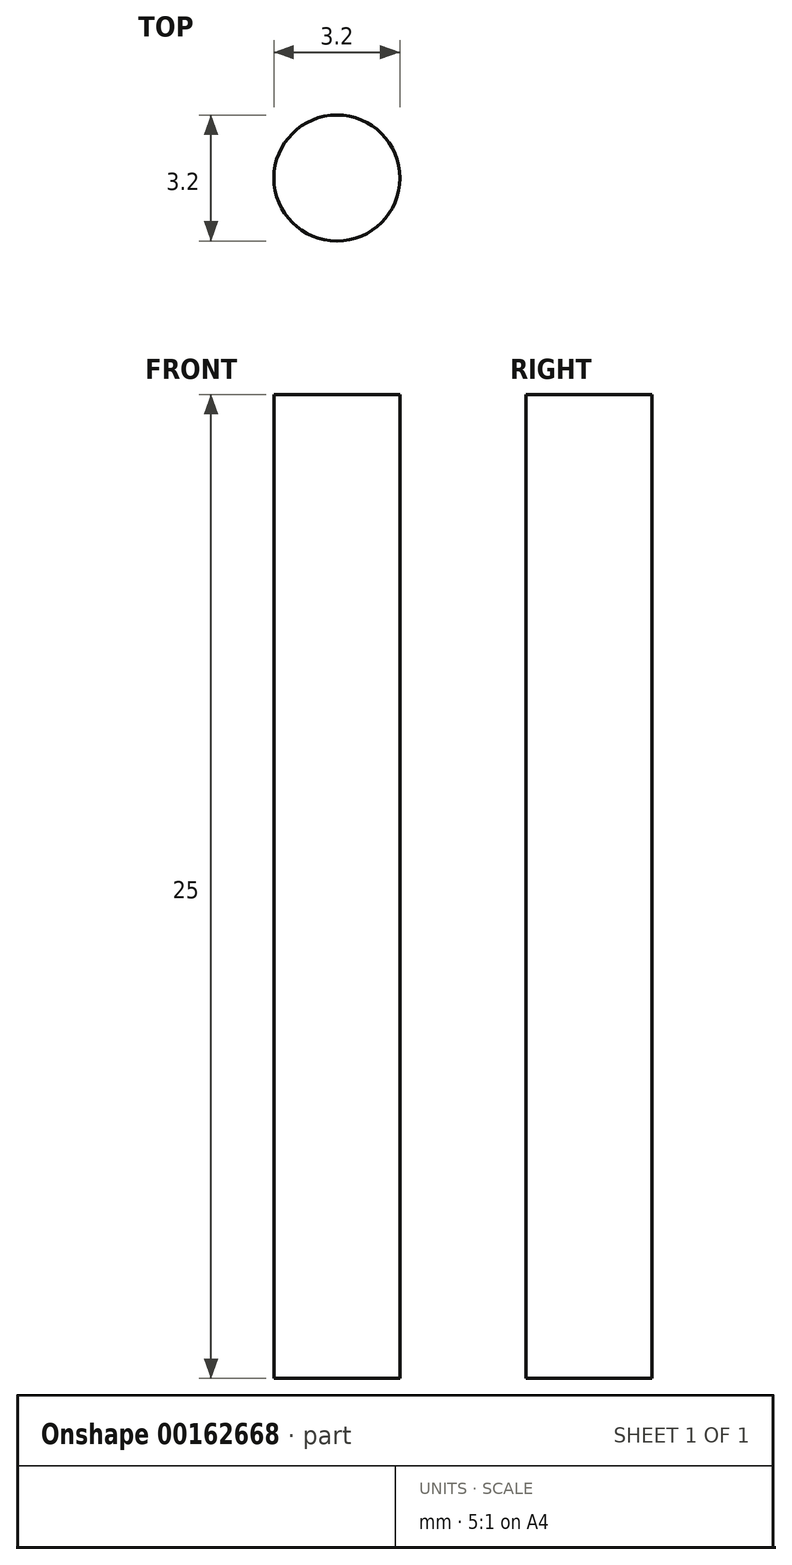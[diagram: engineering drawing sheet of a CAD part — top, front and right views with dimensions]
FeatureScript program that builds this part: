
annotation { "Feature Type Name" : "Feature", "Feature Type Description" : "" }
export const myFeature = defineFeature(function(context is Context, id is Id, definition is map)
    precondition{}
    {
        {
            var Q0;
            Q0=qCreatedBy(makeId("Top.planeOp"),FACE);
            var sketch = newSketch(context, id + "F0", { "sketchPlane" : qUnion([Q0])});
            skCircle(sketch, "E0", {"center": v(0, 0) * mm, "radius": 1.6 * mm});
            skSolve(sketch);
        }
        {
            var Q0;
            Q0 = qSketchRegion(id + "F0", true);
            extrude(context, id + "F1", {"entities" : qUnion([Q0]), "depth" : 25 * mm, "offsetDistance" : 25 * mm});
        }
    });
